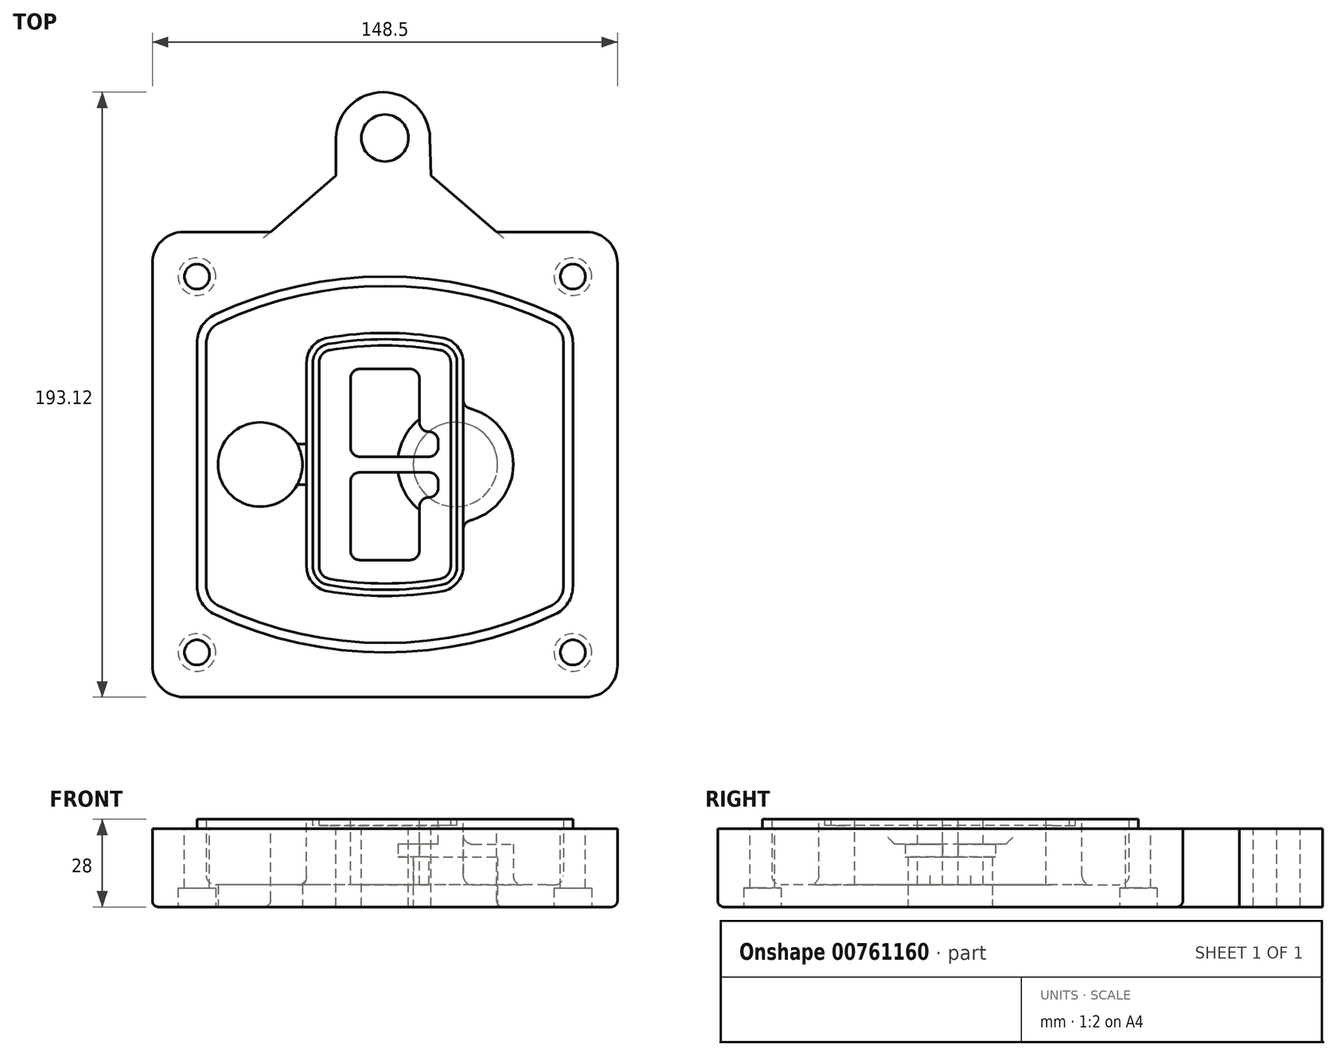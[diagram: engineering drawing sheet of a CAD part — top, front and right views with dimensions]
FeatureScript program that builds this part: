
annotation { "Feature Type Name" : "Feature", "Feature Type Description" : "" }
export const myFeature = defineFeature(function(context is Context, id is Id, definition is map)
    precondition{}
    {
        {
            var Q0;
            Q0=qCreatedBy(makeId("Top.planeOp"),FACE);
            var sketch = newSketch(context, id + "F0", { "sketchPlane" : qUnion([Q0])});
            skPoint(sketch, "E0.rect.middle", {"position": v(0, 0) * mm});
            skLineSegment(sketch, "E1.bottom", {"start": v(-64.25, -74.25) * mm, "end": v(64.25, -74.25) * mm});
            skLineSegment(sketch, "E1.top", {"start": v(-64.25, 74.25) * mm, "end": v(64.25, 74.25) * mm});
            skLineSegment(sketch, "E1.left", {"start": v(-74.25, -64.25) * mm, "end": v(-74.25, 64.25) * mm});
            skLineSegment(sketch, "E1.right", {"start": v(74.25, -64.25) * mm, "end": v(74.25, 64.25) * mm});
            skLineSegment(sketch, "E2", {"start": v(-74.25, 74.25) * mm, "end": v(74.25, -74.25) * mm, "construction": true});
            skLineSegment(sketch, "E3", {"start": v(74.25, 74.25) * mm, "end": v(-74.25, -74.25) * mm, "construction": true});
            skCircle(sketch, "E4", {"center": v(-60, 60) * mm, "radius": 4 * mm});
            skCircle(sketch, "E5", {"center": v(60, 60) * mm, "radius": 4 * mm});
            skCircle(sketch, "E6", {"center": v(60, -60) * mm, "radius": 4 * mm});
            skCircle(sketch, "E7", {"center": v(-60, -60) * mm, "radius": 4 * mm});
            skLineSegment(sketch, "E8", {"start": v(-60, 60) * mm, "end": v(60, 60) * mm, "construction": true});
            skLineSegment(sketch, "E9", {"start": v(60, 60) * mm, "end": v(60, -60) * mm, "construction": true});
            skLineSegment(sketch, "E10", {"start": v(60, -60) * mm, "end": v(-60, -60) * mm, "construction": true});
            skLineSegment(sketch, "E11", {"start": v(-60, -60) * mm, "end": v(-60, 60) * mm, "construction": true});
            skLineSegment(sketch, "E12", {"start": v(-60, 38.83) * mm, "end": v(-60, -38.83) * mm});
            skLineSegment(sketch, "E13", {"start": v(60, 38.83) * mm, "end": v(60, -38.83) * mm});
            skArc(sketch, "E14", {"start": v(54.26, 47.88) * mm, "mid": v(0, 60) * mm, "end": v(-54.26, 47.88) * mm});
            skArc(sketch, "E15", {"start": v(-54.26, -47.88) * mm, "mid": v(0, -60) * mm, "end": v(54.26, -47.88) * mm});
            skLineSegment(sketch, "E16", {"start": v(-60, 0) * mm, "end": v(60, 0) * mm, "construction": true});
            skPoint(sketch, "E17.visualSharp", {"position": v(-60, -45) * mm});
            skArc(sketch, "E17.filletArc", {"start": v(-60, -38.83) * mm, "mid": v(-58.44, -44.2) * mm, "end": v(-54.26, -47.88) * mm});
            skPoint(sketch, "E18.visualSharp", {"position": v(-60, 45) * mm});
            skArc(sketch, "E18.filletArc", {"start": v(-54.26, 47.88) * mm, "mid": v(-58.44, 44.2) * mm, "end": v(-60, 38.83) * mm});
            skPoint(sketch, "E19.visualSharp", {"position": v(60, 45) * mm});
            skArc(sketch, "E19.filletArc", {"start": v(60, 38.83) * mm, "mid": v(58.44, 44.2) * mm, "end": v(54.26, 47.88) * mm});
            skPoint(sketch, "E20.visualSharp", {"position": v(60, -45) * mm});
            skArc(sketch, "E20.filletArc", {"start": v(54.26, -47.88) * mm, "mid": v(58.44, -44.2) * mm, "end": v(60, -38.83) * mm});
            skPoint(sketch, "E21.visualSharp", {"position": v(-74.25, 74.25) * mm});
            skArc(sketch, "E21.filletArc", {"start": v(-64.25, 74.25) * mm, "mid": v(-71.32, 71.32) * mm, "end": v(-74.25, 64.25) * mm});
            skPoint(sketch, "E22.visualSharp", {"position": v(74.25, 74.25) * mm});
            skArc(sketch, "E22.filletArc", {"start": v(74.25, 64.25) * mm, "mid": v(71.32, 71.32) * mm, "end": v(64.25, 74.25) * mm});
            skPoint(sketch, "E23.visualSharp", {"position": v(74.25, -74.25) * mm});
            skArc(sketch, "E23.filletArc", {"start": v(64.25, -74.25) * mm, "mid": v(71.32, -71.32) * mm, "end": v(74.25, -64.25) * mm});
            skPoint(sketch, "E24.visualSharp", {"position": v(-74.25, -74.25) * mm});
            skArc(sketch, "E24.filletArc", {"start": v(-74.25, -64.25) * mm, "mid": v(-71.32, -71.32) * mm, "end": v(-64.25, -74.25) * mm});
            skArc(sketch, "E25.0", {"start": v(57, 38.83) * mm, "mid": v(55.9, 42.58) * mm, "end": v(52.98, 45.17) * mm});
            skLineSegment(sketch, "E25.1", {"start": v(57, 38.83) * mm, "end": v(57, -38.83) * mm});
            skArc(sketch, "E25.2", {"start": v(52.98, -45.17) * mm, "mid": v(55.9, -42.58) * mm, "end": v(57, -38.83) * mm});
            skArc(sketch, "E25.3", {"start": v(-52.98, -45.17) * mm, "mid": v(0, -57) * mm, "end": v(52.98, -45.17) * mm});
            skArc(sketch, "E25.4", {"start": v(-57, -38.83) * mm, "mid": v(-55.9, -42.58) * mm, "end": v(-52.98, -45.17) * mm});
            skArc(sketch, "E25.5", {"start": v(52.98, 45.17) * mm, "mid": v(0, 57) * mm, "end": v(-52.98, 45.17) * mm});
            skLineSegment(sketch, "E25.6", {"start": v(-57, 38.83) * mm, "end": v(-57, -38.83) * mm});
            skArc(sketch, "E25.7", {"start": v(-52.98, 45.17) * mm, "mid": v(-55.9, 42.58) * mm, "end": v(-57, 38.83) * mm});
            skArc(sketch, "E26.0", {"start": v(-55.96, 51.5) * mm, "mid": v(-61.82, 46.33) * mm, "end": v(-64, 38.83) * mm});
            skArc(sketch, "E26.1", {"start": v(55.96, 51.5) * mm, "mid": v(0, 64) * mm, "end": v(-55.96, 51.5) * mm});
            skArc(sketch, "E26.2", {"start": v(64, 38.83) * mm, "mid": v(61.82, 46.33) * mm, "end": v(55.96, 51.5) * mm});
            skLineSegment(sketch, "E26.3", {"start": v(64, 38.83) * mm, "end": v(64, -38.83) * mm});
            skArc(sketch, "E26.4", {"start": v(55.96, -51.5) * mm, "mid": v(61.82, -46.33) * mm, "end": v(64, -38.83) * mm});
            skLineSegment(sketch, "E26.5", {"start": v(-64, 38.83) * mm, "end": v(-64, -38.83) * mm});
            skArc(sketch, "E26.6", {"start": v(-55.96, -51.5) * mm, "mid": v(0, -64) * mm, "end": v(55.96, -51.5) * mm});
            skArc(sketch, "E26.7", {"start": v(-64, -38.83) * mm, "mid": v(-61.82, -46.33) * mm, "end": v(-55.96, -51.5) * mm});
            skCircle(sketch, "E27", {"center": v(0, 104.25) * mm, "radius": 7.5 * mm});
            skPoint(sketch, "E27.centerSnap0", {"position": v(0, 74.25) * mm});
            skArc(sketch, "E28", {"start": v(14.38, 104.25) * mm, "mid": v(-0.61, 118.87) * mm, "end": v(-15.6, 104.25) * mm});
            skLineSegment(sketch, "E29", {"start": v(-15.6, 104.25) * mm, "end": v(-15.6, 92.25) * mm});
            skLineSegment(sketch, "E30", {"start": v(14.38, 104.25) * mm, "end": v(14.7, 92.25) * mm});
            skLineSegment(sketch, "E31", {"start": v(-15.6, 92.25) * mm, "end": v(-36.52, 74.25) * mm});
            skLineSegment(sketch, "E32", {"start": v(14.7, 92.25) * mm, "end": v(35.6, 74.25) * mm});
            skArc(sketch, "E33.MirrorCS", {"start": v(14.38, -252.75) * mm, "mid": v(-0.61, -267.37) * mm, "end": v(-15.6, -252.75) * mm});
            skLineSegment(sketch, "E34.MirrorCS", {"start": v(14.7, -240.75) * mm, "end": v(35.6, -222.75) * mm});
            skLineSegment(sketch, "E35.MirrorCS", {"start": v(-15.6, -240.75) * mm, "end": v(-36.52, -222.75) * mm});
            skLineSegment(sketch, "E36.MirrorCS", {"start": v(14.38, -252.75) * mm, "end": v(14.7, -240.75) * mm});
            skLineSegment(sketch, "E37.MirrorCS", {"start": v(-15.6, -252.75) * mm, "end": v(-15.6, -240.75) * mm});
            skCircle(sketch, "E38.MirrorC", {"center": v(0, -252.75) * mm, "radius": 7.5 * mm});
            skPoint(sketch, "E39.MirrorP", {"position": v(0, -222.75) * mm});
            skSolve(sketch);
        }
        {
            var Q0;
            Q0=makeQuery(id+"F0.imprint","IMPRINT",FACE,{"disambiguationData":[TD([[makeQuery(id+"F0.imprint","IMPRINT",EDGE,{"derivedFrom":sQuery(id+"F0.wireOp",EDGE,"E1.bottom")}),1.0]])]});
            var Q1;
            Q1=makeQuery(id+"F0.imprint","IMPRINT",FACE,{"disambiguationData":[TD([[makeQuery(id+"F0.imprint","IMPRINT",EDGE,{"derivedFrom":sQuery(id+"F0.wireOp",EDGE,"E12")}),1.0]])]});
            var Q2;
            Q2=makeQuery(id+"F0.imprint","IMPRINT",FACE,{"disambiguationData":[TD([[makeQuery(id+"F0.imprint","IMPRINT",EDGE,{"derivedFrom":sQuery(id+"F0.wireOp",EDGE,"E25.0")}),1.0]])]});
            var Q3;
            Q3=makeQuery(id+"F0.imprint","IMPRINT",FACE,{"disambiguationData":[TD([[makeQuery(id+"F0.imprint","IMPRINT",EDGE,{"derivedFrom":sQuery(id+"F0.wireOp",EDGE,"E12")}),-1.0]])]});
            var Q4;
            Q4=makeQuery(id+"F0.imprint","IMPRINT",FACE,{"disambiguationData":[TD([[makeQuery(id+"F0.imprint","IMPRINT",EDGE,{"derivedFrom":sQuery(id+"F0.wireOp",EDGE,"E27")}),-1.0]])]});
            var Q5;
            {var subQ0=sQuery(id+"F0.wireOp",EDGE,"E32");var subQ1=sQuery(id+"F0.wireOp",EDGE,"E1.top");var subQ2=makeQuery(id+"F0.imprint","INTERSECT",VERTEX,{"derivedFrom":[subQ1,subQ0]});Q5=makeQuery(id+"F0.imprint","IMPRINT",FACE,{"disambiguationData":[TD([[makeQuery(id+"F0.imprint","IMPRINT",EDGE,{"disambiguationData":[TD([[subQ2,1.0]])],"derivedFrom":subQ1}),1.0]])]});}
            extrude(context, id + "F1", {"entities" : qUnion([Q0, Q1, Q2, Q3, Q4, Q5]), "oppositeDirection" : true, "depth" : 25 * mm, "offsetDistance" : 25 * mm});
        }
        {
            var Q0;
            Q0=makeQuery(id+"F0.imprint","IMPRINT",FACE,{"disambiguationData":[TD([[makeQuery(id+"F0.imprint","IMPRINT",EDGE,{"derivedFrom":sQuery(id+"F0.wireOp",EDGE,"E12")}),1.0]])]});
            extrude(context, id + "F2", {"entities" : qUnion([Q0]), "operationType" : NewBodyOperationType.ADD, "depth" : 3 * mm});
        }
        {
            var Q0;
            Q0=makeQuery(id+"F0.imprint","IMPRINT",FACE,{"disambiguationData":[TD([[makeQuery(id+"F0.imprint","IMPRINT",EDGE,{"derivedFrom":sQuery(id+"F0.wireOp",EDGE,"E25.0")}),1.0]])]});
            extrude(context, id + "F3", {"entities" : qUnion([Q0]), "operationType" : NewBodyOperationType.REMOVE, "oppositeDirection" : true, "depth" : 18 * mm});
        }
        {
            var Q0;
            Q0=makeQuery(id+"F2.opExtrude","CAP_FACE",FACE,{"disambiguationData":[OSD([sQuery(id+"F0.wireOp",EDGE,"E12"),sQuery(id+"F0.wireOp",EDGE,"E13"),sQuery(id+"F0.wireOp",EDGE,"E14"),sQuery(id+"F0.wireOp",EDGE,"E15"),sQuery(id+"F0.wireOp",EDGE,"E17.filletArc"),sQuery(id+"F0.wireOp",EDGE,"E18.filletArc"),sQuery(id+"F0.wireOp",EDGE,"E19.filletArc"),sQuery(id+"F0.wireOp",EDGE,"E20.filletArc"),sQuery(id+"F0.wireOp",EDGE,"E25.0"),sQuery(id+"F0.wireOp",EDGE,"E25.1"),sQuery(id+"F0.wireOp",EDGE,"E25.2"),sQuery(id+"F0.wireOp",EDGE,"E25.3"),sQuery(id+"F0.wireOp",EDGE,"E25.4"),sQuery(id+"F0.wireOp",EDGE,"E25.5"),sQuery(id+"F0.wireOp",EDGE,"E25.6"),sQuery(id+"F0.wireOp",EDGE,"E25.7")])],"isStart":false});
            var sketch = newSketch(context, id + "F4", { "sketchPlane" : qUnion([Q0])});
            skArc(sketch, "E40.0", {"start": v(-18.34, -40.45) * mm, "mid": v(0, -42) * mm, "end": v(18.34, -40.45) * mm});
            skArc(sketch, "E41.0", {"start": v(18.34, 40.45) * mm, "mid": v(0, 42) * mm, "end": v(-18.34, 40.45) * mm});
            skLineSegment(sketch, "E42", {"start": v(-25, 32.57) * mm, "end": v(-25, -32.57) * mm});
            skLineSegment(sketch, "E43", {"start": v(25, 32.57) * mm, "end": v(25, -32.57) * mm});
            skLineSegment(sketch, "E44", {"start": v(-25, 39.1) * mm, "end": v(25, 39.1) * mm, "construction": true});
            skLineSegment(sketch, "E45", {"start": v(-25, -39.1) * mm, "end": v(25, -39.1) * mm, "construction": true});
            skPoint(sketch, "E46.visualSharp", {"position": v(-25, 39.1) * mm});
            skArc(sketch, "E46.filletArc", {"start": v(-18.34, 40.45) * mm, "mid": v(-23.11, 37.73) * mm, "end": v(-25, 32.57) * mm});
            skPoint(sketch, "E47.visualSharp", {"position": v(25, 39.1) * mm});
            skArc(sketch, "E47.filletArc", {"start": v(25, 32.57) * mm, "mid": v(23.11, 37.73) * mm, "end": v(18.34, 40.45) * mm});
            skPoint(sketch, "E48.visualSharp", {"position": v(25, -39.1) * mm});
            skArc(sketch, "E48.filletArc", {"start": v(18.34, -40.45) * mm, "mid": v(23.11, -37.73) * mm, "end": v(25, -32.57) * mm});
            skPoint(sketch, "E49.visualSharp", {"position": v(-25, -39.1) * mm});
            skArc(sketch, "E49.filletArc", {"start": v(-25, -32.57) * mm, "mid": v(-23.11, -37.73) * mm, "end": v(-18.34, -40.45) * mm});
            skArc(sketch, "E50.0", {"start": v(52.98, 45.17) * mm, "mid": v(0, 57) * mm, "end": v(-52.98, 45.17) * mm});
            skArc(sketch, "E50.1", {"start": v(-52.98, 45.17) * mm, "mid": v(-55.9, 42.58) * mm, "end": v(-57, 38.83) * mm});
            skLineSegment(sketch, "E50.2", {"start": v(-57, 38.83) * mm, "end": v(-57, -38.83) * mm});
            skArc(sketch, "E50.3", {"start": v(-57, -38.83) * mm, "mid": v(-55.9, -42.58) * mm, "end": v(-52.98, -45.17) * mm});
            skArc(sketch, "E50.4", {"start": v(-52.98, -45.17) * mm, "mid": v(0, -57) * mm, "end": v(52.98, -45.17) * mm});
            skArc(sketch, "E50.5", {"start": v(52.98, -45.17) * mm, "mid": v(55.9, -42.58) * mm, "end": v(57, -38.83) * mm});
            skLineSegment(sketch, "E50.6", {"start": v(57, 38.83) * mm, "end": v(57, -38.83) * mm});
            skArc(sketch, "E50.7", {"start": v(57, 38.83) * mm, "mid": v(55.9, 42.58) * mm, "end": v(52.98, 45.17) * mm});
            skLineSegment(sketch, "E51.0", {"start": v(23, 32.57) * mm, "end": v(23, -32.57) * mm});
            skArc(sketch, "E51.1", {"start": v(18, -38.48) * mm, "mid": v(21.58, -36.44) * mm, "end": v(23, -32.57) * mm});
            skArc(sketch, "E51.2", {"start": v(-18, -38.48) * mm, "mid": v(0, -40) * mm, "end": v(18, -38.48) * mm});
            skArc(sketch, "E51.3", {"start": v(-23, -32.57) * mm, "mid": v(-21.58, -36.44) * mm, "end": v(-18, -38.48) * mm});
            skLineSegment(sketch, "E51.4", {"start": v(-23, 32.57) * mm, "end": v(-23, -32.57) * mm});
            skArc(sketch, "E51.5", {"start": v(23, 32.57) * mm, "mid": v(21.58, 36.44) * mm, "end": v(18, 38.48) * mm});
            skArc(sketch, "E51.6", {"start": v(-18, 38.48) * mm, "mid": v(-21.58, 36.44) * mm, "end": v(-23, 32.57) * mm});
            skArc(sketch, "E51.7", {"start": v(18, 38.48) * mm, "mid": v(0, 40) * mm, "end": v(-18, 38.48) * mm});
            skArc(sketch, "E52.0", {"start": v(21, 32.57) * mm, "mid": v(20.06, 35.15) * mm, "end": v(17.67, 36.5) * mm});
            skLineSegment(sketch, "E52.1", {"start": v(21, 32.57) * mm, "end": v(21, -32.57) * mm});
            skArc(sketch, "E52.2", {"start": v(17.67, -36.5) * mm, "mid": v(20.06, -35.15) * mm, "end": v(21, -32.57) * mm});
            skArc(sketch, "E52.3", {"start": v(-17.67, -36.5) * mm, "mid": v(0, -38) * mm, "end": v(17.67, -36.5) * mm});
            skArc(sketch, "E52.4", {"start": v(-21, -32.57) * mm, "mid": v(-20.06, -35.15) * mm, "end": v(-17.67, -36.5) * mm});
            skArc(sketch, "E52.5", {"start": v(17.67, 36.5) * mm, "mid": v(0, 38) * mm, "end": v(-17.67, 36.5) * mm});
            skLineSegment(sketch, "E52.6", {"start": v(-21, 32.57) * mm, "end": v(-21, -32.57) * mm});
            skArc(sketch, "E52.7", {"start": v(-17.67, 36.5) * mm, "mid": v(-20.06, 35.15) * mm, "end": v(-21, 32.57) * mm});
            skLineSegment(sketch, "E53", {"start": v(-25, 0) * mm, "end": v(25, 0) * mm, "construction": true});
            skLineSegment(sketch, "E54", {"start": v(-11, 5.5) * mm, "end": v(-11, 27.5) * mm});
            skLineSegment(sketch, "E55", {"start": v(-8, 30.5) * mm, "end": v(8, 30.5) * mm});
            skLineSegment(sketch, "E56", {"start": v(11, 27.5) * mm, "end": v(11, 13.5) * mm});
            skLineSegment(sketch, "E57", {"start": v(14, 10.5) * mm, "end": v(14, 10.5) * mm});
            skLineSegment(sketch, "E58", {"start": v(17, 7.5) * mm, "end": v(17, 5.5) * mm});
            skLineSegment(sketch, "E59", {"start": v(14, 2.5) * mm, "end": v(-8, 2.5) * mm});
            skPoint(sketch, "E60.visualSharp", {"position": v(-11, 30.5) * mm});
            skArc(sketch, "E60.filletArc", {"start": v(-8, 30.5) * mm, "mid": v(-10.12, 29.62) * mm, "end": v(-11, 27.5) * mm});
            skPoint(sketch, "E61.visualSharp", {"position": v(11, 30.5) * mm});
            skArc(sketch, "E61.filletArc", {"start": v(11, 27.5) * mm, "mid": v(10.12, 29.62) * mm, "end": v(8, 30.5) * mm});
            skPoint(sketch, "E62.visualSharp", {"position": v(11, 10.5) * mm});
            skArc(sketch, "E62.filletArc", {"start": v(11, 13.5) * mm, "mid": v(11.88, 11.38) * mm, "end": v(14, 10.5) * mm});
            skPoint(sketch, "E63.visualSharp", {"position": v(17, 10.5) * mm});
            skArc(sketch, "E63.filletArc", {"start": v(17, 7.5) * mm, "mid": v(16.12, 9.62) * mm, "end": v(14, 10.5) * mm});
            skPoint(sketch, "E64.visualSharp", {"position": v(17, 2.5) * mm});
            skArc(sketch, "E64.filletArc", {"start": v(14, 2.5) * mm, "mid": v(16.12, 3.38) * mm, "end": v(17, 5.5) * mm});
            skPoint(sketch, "E65.visualSharp", {"position": v(-11, 2.5) * mm});
            skArc(sketch, "E65.filletArc", {"start": v(-11, 5.5) * mm, "mid": v(-10.12, 3.38) * mm, "end": v(-8, 2.5) * mm});
            skLineSegment(sketch, "E66.0.MirrorCS", {"start": v(14, -2.5) * mm, "end": v(-8, -2.5) * mm});
            skArc(sketch, "E67.0.MirrorCS", {"start": v(-11, -5.5) * mm, "mid": v(-10.12, -3.38) * mm, "end": v(-8, -2.5) * mm});
            skLineSegment(sketch, "E68.0.MirrorCS", {"start": v(-11, -5.5) * mm, "end": v(-11, -27.5) * mm});
            skArc(sketch, "E69.0.MirrorCS", {"start": v(-8, -30.5) * mm, "mid": v(-10.12, -29.62) * mm, "end": v(-11, -27.5) * mm});
            skLineSegment(sketch, "E70.0.MirrorCS", {"start": v(-8, -30.5) * mm, "end": v(8, -30.5) * mm});
            skArc(sketch, "E71.0.MirrorCS", {"start": v(11, -27.5) * mm, "mid": v(10.12, -29.62) * mm, "end": v(8, -30.5) * mm});
            skLineSegment(sketch, "E72.0.MirrorCS", {"start": v(11, -27.5) * mm, "end": v(11, -13.5) * mm});
            skArc(sketch, "E73.0.MirrorCS", {"start": v(11, -13.5) * mm, "mid": v(11.88, -11.38) * mm, "end": v(14, -10.5) * mm});
            skArc(sketch, "E74.0.MirrorCS", {"start": v(17, -7.5) * mm, "mid": v(16.12, -9.62) * mm, "end": v(14, -10.5) * mm});
            skLineSegment(sketch, "E75.0.MirrorCS", {"start": v(17, -7.5) * mm, "end": v(17, -5.5) * mm});
            skArc(sketch, "E76.0.MirrorCS", {"start": v(14, -2.5) * mm, "mid": v(16.12, -3.38) * mm, "end": v(17, -5.5) * mm});
            skSolve(sketch);
        }
        {
            var Q0;
            Q0=makeQuery(id+"F4.imprint","IMPRINT",FACE,{"disambiguationData":[TD([[makeQuery(id+"F4.imprint","IMPRINT",EDGE,{"derivedFrom":sQuery(id+"F4.wireOp",EDGE,"E40.0")}),1.0]])]});
            var Q1;
            Q1=makeQuery(id+"F4.imprint","IMPRINT",FACE,{"disambiguationData":[TD([[makeQuery(id+"F4.imprint","IMPRINT",EDGE,{"derivedFrom":sQuery(id+"F4.wireOp",EDGE,"E51.0")}),-1.0]])]});
            var Q2;
            Q2=makeQuery(id+"F4.imprint","IMPRINT",FACE,{"disambiguationData":[TD([[makeQuery(id+"F4.imprint","IMPRINT",EDGE,{"derivedFrom":sQuery(id+"F4.wireOp",EDGE,"E52.0")}),1.0]])]});
            extrude(context, id + "F5", {"entities" : qUnion([Q0, Q1, Q2]), "operationType" : NewBodyOperationType.ADD, "endBound" : BoundingType.UP_TO_NEXT, "oppositeDirection" : true, "depth" : 25 * mm});
        }
        {
            var Q0;
            Q0=makeQuery(id+"F4.imprint","IMPRINT",FACE,{"disambiguationData":[TD([[makeQuery(id+"F4.imprint","IMPRINT",EDGE,{"derivedFrom":sQuery(id+"F4.wireOp",EDGE,"E51.0")}),-1.0]])]});
            extrude(context, id + "F6", {"entities" : qUnion([Q0]), "operationType" : NewBodyOperationType.REMOVE, "oppositeDirection" : true, "depth" : 2 * mm});
        }
        {
            var Q0;
            Q0=makeQuery(id+"F1.opExtrude","CAP_FACE",FACE,{"disambiguationData":[OSD([sQuery(id+"F0.wireOp",EDGE,"E1.bottom"),sQuery(id+"F0.wireOp",EDGE,"E1.top"),sQuery(id+"F0.wireOp",EDGE,"E1.left"),sQuery(id+"F0.wireOp",EDGE,"E1.right"),sQuery(id+"F0.wireOp",EDGE,"E4"),sQuery(id+"F0.wireOp",EDGE,"E5"),sQuery(id+"F0.wireOp",EDGE,"E6"),sQuery(id+"F0.wireOp",EDGE,"E7"),sQuery(id+"F0.wireOp",EDGE,"E21.filletArc"),sQuery(id+"F0.wireOp",EDGE,"E22.filletArc"),sQuery(id+"F0.wireOp",EDGE,"E23.filletArc"),sQuery(id+"F0.wireOp",EDGE,"E24.filletArc")])],"isStart":false});
            var sketch = newSketch(context, id + "F7", { "sketchPlane" : qUnion([Q0])});
            skCircle(sketch, "E77", {"center": v(22.5, 0) * mm, "radius": 13.47 * mm});
            skCircle(sketch, "E78", {"center": v(-39.81, 0) * mm, "radius": 13.47 * mm});
            skLineSegment(sketch, "E79", {"start": v(74.25, 0) * mm, "end": v(-74.25, 0) * mm});
            skCircle(sketch, "E80", {"center": v(22.5, 0) * mm, "radius": 18.47 * mm});
            skCircle(sketch, "E81", {"center": v(60, -60) * mm, "radius": 6 * mm});
            skCircle(sketch, "E82", {"center": v(-60, -60) * mm, "radius": 6 * mm});
            skCircle(sketch, "E83", {"center": v(-60, 60) * mm, "radius": 6 * mm});
            skCircle(sketch, "E84", {"center": v(60, 60) * mm, "radius": 6 * mm});
            skSolve(sketch);
        }
        {
            var Q0;
            {var subQ1=sQuery(id+"F7.wireOp",EDGE,"E79");var subQ4=sQuery(id+"F7.wireOp",EDGE,"E77");var subQ6=makeQuery(id+"F7.imprint","INTERSECT",VERTEX,{"disambiguationData":[OD(0.0)],"derivedFrom":[subQ4,subQ1]});Q0=makeQuery(id+"F7.imprint","IMPRINT",FACE,{"disambiguationData":[TD([[makeQuery(id+"F7.imprint","IMPRINT",EDGE,{"disambiguationData":[TD([[subQ6,-1.0]])],"derivedFrom":subQ4}),-1.0]])]});}
            var Q1;
            {var subQ0=sQuery(id+"F7.wireOp",EDGE,"E79");var subQ1=sQuery(id+"F7.wireOp",EDGE,"E77");var subQ3=makeQuery(id+"F7.imprint","INTERSECT",VERTEX,{"disambiguationData":[OD(0.0)],"derivedFrom":[subQ1,subQ0]});Q1=makeQuery(id+"F7.imprint","IMPRINT",FACE,{"disambiguationData":[TD([[makeQuery(id+"F7.imprint","IMPRINT",EDGE,{"disambiguationData":[TD([[subQ3,-1.0]])],"derivedFrom":subQ1}),1.0]])]});}
            var Q2;
            {var subQ0=sQuery(id+"F7.wireOp",EDGE,"E79");var subQ1=sQuery(id+"F7.wireOp",EDGE,"E77");var subQ3=makeQuery(id+"F7.imprint","INTERSECT",VERTEX,{"disambiguationData":[OD(0.0)],"derivedFrom":[subQ1,subQ0]});Q2=makeQuery(id+"F7.imprint","IMPRINT",FACE,{"disambiguationData":[TD([[makeQuery(id+"F7.imprint","IMPRINT",EDGE,{"disambiguationData":[TD([[subQ3,1.0]])],"derivedFrom":subQ1}),1.0]])]});}
            var Q3;
            {var subQ1=sQuery(id+"F7.wireOp",EDGE,"E79");var subQ4=sQuery(id+"F7.wireOp",EDGE,"E77");var subQ6=makeQuery(id+"F7.imprint","INTERSECT",VERTEX,{"disambiguationData":[OD(0.0)],"derivedFrom":[subQ4,subQ1]});Q3=makeQuery(id+"F7.imprint","IMPRINT",FACE,{"disambiguationData":[TD([[makeQuery(id+"F7.imprint","IMPRINT",EDGE,{"disambiguationData":[TD([[subQ6,1.0]])],"derivedFrom":subQ4}),-1.0]])]});}
            extrude(context, id + "F8", {"entities" : qUnion([Q0, Q1, Q2, Q3]), "operationType" : NewBodyOperationType.ADD, "oppositeDirection" : true, "depth" : 20 * mm});
        }
        {
            var Q0;
            {var subQ0=sQuery(id+"F7.wireOp",EDGE,"E79");var subQ1=sQuery(id+"F7.wireOp",EDGE,"E77");var subQ3=makeQuery(id+"F7.imprint","INTERSECT",VERTEX,{"disambiguationData":[OD(0.0)],"derivedFrom":[subQ1,subQ0]});Q0=makeQuery(id+"F7.imprint","IMPRINT",FACE,{"disambiguationData":[TD([[makeQuery(id+"F7.imprint","IMPRINT",EDGE,{"disambiguationData":[TD([[subQ3,-1.0]])],"derivedFrom":subQ1}),1.0]])]});}
            var Q1;
            {var subQ0=sQuery(id+"F7.wireOp",EDGE,"E79");var subQ1=sQuery(id+"F7.wireOp",EDGE,"E77");var subQ3=makeQuery(id+"F7.imprint","INTERSECT",VERTEX,{"disambiguationData":[OD(0.0)],"derivedFrom":[subQ1,subQ0]});Q1=makeQuery(id+"F7.imprint","IMPRINT",FACE,{"disambiguationData":[TD([[makeQuery(id+"F7.imprint","IMPRINT",EDGE,{"disambiguationData":[TD([[subQ3,1.0]])],"derivedFrom":subQ1}),1.0]])]});}
            extrude(context, id + "F9", {"entities" : qUnion([Q0, Q1]), "operationType" : NewBodyOperationType.REMOVE, "oppositeDirection" : true, "depth" : 16 * mm});
        }
        {
            var Q0;
            {var subQ0=sQuery(id+"F7.wireOp",EDGE,"E79");var subQ1=sQuery(id+"F7.wireOp",EDGE,"E78");var subQ3=makeQuery(id+"F7.imprint","INTERSECT",VERTEX,{"disambiguationData":[OD(0.0)],"derivedFrom":[subQ1,subQ0]});Q0=makeQuery(id+"F7.imprint","IMPRINT",FACE,{"disambiguationData":[TD([[makeQuery(id+"F7.imprint","IMPRINT",EDGE,{"disambiguationData":[TD([[subQ3,-1.0]])],"derivedFrom":subQ1}),1.0]])]});}
            var Q1;
            {var subQ0=sQuery(id+"F7.wireOp",EDGE,"E79");var subQ1=sQuery(id+"F7.wireOp",EDGE,"E78");var subQ3=makeQuery(id+"F7.imprint","INTERSECT",VERTEX,{"disambiguationData":[OD(0.0)],"derivedFrom":[subQ1,subQ0]});Q1=makeQuery(id+"F7.imprint","IMPRINT",FACE,{"disambiguationData":[TD([[makeQuery(id+"F7.imprint","IMPRINT",EDGE,{"disambiguationData":[TD([[subQ3,1.0]])],"derivedFrom":subQ1}),1.0]])]});}
            extrude(context, id + "F10", {"entities" : qUnion([Q0, Q1]), "operationType" : NewBodyOperationType.REMOVE, "oppositeDirection" : true, "depth" : 25 * mm});
        }
        {
            var Q0;
            Q0=makeQuery(id+"F7.imprint","IMPRINT",FACE,{"disambiguationData":[TD([[makeQuery(id+"F7.imprint","IMPRINT",EDGE,{"derivedFrom":sQuery(id+"F7.wireOp",EDGE,"E81")}),1.0]])]});
            var Q1;
            Q1=makeQuery(id+"F7.imprint","IMPRINT",FACE,{"disambiguationData":[TD([[makeQuery(id+"F7.imprint","IMPRINT",EDGE,{"derivedFrom":makeQuery(id+"F1.opExtrude","CAP_EDGE",EDGE,{"disambiguationData":[OSD([sQuery(id+"F0.wireOp",EDGE,"E5")])],"isStart":false})}),-1.0]])]});
            var Q2;
            Q2=makeQuery(id+"F7.imprint","IMPRINT",FACE,{"disambiguationData":[TD([[makeQuery(id+"F7.imprint","IMPRINT",EDGE,{"derivedFrom":sQuery(id+"F7.wireOp",EDGE,"E82")}),1.0]])]});
            var Q3;
            Q3=makeQuery(id+"F7.imprint","IMPRINT",FACE,{"disambiguationData":[TD([[makeQuery(id+"F7.imprint","IMPRINT",EDGE,{"derivedFrom":makeQuery(id+"F1.opExtrude","CAP_EDGE",EDGE,{"disambiguationData":[OSD([sQuery(id+"F0.wireOp",EDGE,"E4")])],"isStart":false})}),-1.0]])]});
            var Q4;
            Q4=makeQuery(id+"F7.imprint","IMPRINT",FACE,{"disambiguationData":[TD([[makeQuery(id+"F7.imprint","IMPRINT",EDGE,{"derivedFrom":sQuery(id+"F7.wireOp",EDGE,"E83")}),1.0]])]});
            var Q5;
            Q5=makeQuery(id+"F7.imprint","IMPRINT",FACE,{"disambiguationData":[TD([[makeQuery(id+"F7.imprint","IMPRINT",EDGE,{"derivedFrom":makeQuery(id+"F1.opExtrude","CAP_EDGE",EDGE,{"disambiguationData":[OSD([sQuery(id+"F0.wireOp",EDGE,"E7")])],"isStart":false})}),-1.0]])]});
            var Q6;
            Q6=makeQuery(id+"F7.imprint","IMPRINT",FACE,{"disambiguationData":[TD([[makeQuery(id+"F7.imprint","IMPRINT",EDGE,{"derivedFrom":sQuery(id+"F7.wireOp",EDGE,"E84")}),1.0]])]});
            var Q7;
            Q7=makeQuery(id+"F7.imprint","IMPRINT",FACE,{"disambiguationData":[TD([[makeQuery(id+"F7.imprint","IMPRINT",EDGE,{"derivedFrom":makeQuery(id+"F1.opExtrude","CAP_EDGE",EDGE,{"disambiguationData":[OSD([sQuery(id+"F0.wireOp",EDGE,"E6")])],"isStart":false})}),-1.0]])]});
            extrude(context, id + "F11", {"entities" : qUnion([Q0, Q1, Q2, Q3, Q4, Q5, Q6, Q7]), "operationType" : NewBodyOperationType.REMOVE, "oppositeDirection" : true, "depth" : 6 * mm});
        }
        {
            var Q0;
            Q0=makeQuery(id+"F9.boolean.opBoolean","COPY",FACE,{"derivedFrom":makeQuery(id+"F9.opExtrude","CAP_FACE",FACE,{"disambiguationData":[OSD([sQuery(id+"F7.wireOp",EDGE,"E77")])],"isStart":false})});
            var sketch = newSketch(context, id + "F12", { "sketchPlane" : qUnion([Q0])});
            skArc(sketch, "E85.0", {"start": v(11, 14.45) * mm, "mid": v(6.45, 9.13) * mm, "end": v(4.2, 2.5) * mm});
            skArc(sketch, "E85.1", {"start": v(4.2, -2.5) * mm, "mid": v(6.45, -9.13) * mm, "end": v(11, -14.45) * mm});
            skLineSegment(sketch, "E86", {"start": v(4.2, -2.5) * mm, "end": v(14, -2.5) * mm});
            skLineSegment(sketch, "E87.0", {"start": v(14, 2.5) * mm, "end": v(4.2, 2.5) * mm});
            skArc(sketch, "E87.1", {"start": v(14, 2.5) * mm, "mid": v(16.12, 3.38) * mm, "end": v(17, 5.5) * mm});
            skLineSegment(sketch, "E87.2", {"start": v(17, 7.5) * mm, "end": v(17, 5.5) * mm});
            skArc(sketch, "E87.3", {"start": v(17, 7.5) * mm, "mid": v(16.12, 9.62) * mm, "end": v(14, 10.5) * mm});
            skArc(sketch, "E87.4", {"start": v(11, 13.5) * mm, "mid": v(11.88, 11.38) * mm, "end": v(14, 10.5) * mm});
            skLineSegment(sketch, "E87.5", {"start": v(11, 14.45) * mm, "end": v(11, 13.5) * mm});
            skLineSegment(sketch, "E87.7", {"start": v(14, -2.5) * mm, "end": v(4.2, -2.5) * mm});
            skArc(sketch, "E87.8", {"start": v(14, -2.5) * mm, "mid": v(16.12, -3.38) * mm, "end": v(17, -5.5) * mm});
            skLineSegment(sketch, "E87.9", {"start": v(17, -7.5) * mm, "end": v(17, -5.5) * mm});
            skArc(sketch, "E87.10", {"start": v(17, -7.5) * mm, "mid": v(16.12, -9.62) * mm, "end": v(14, -10.5) * mm});
            skArc(sketch, "E87.11", {"start": v(11, -13.5) * mm, "mid": v(11.88, -11.38) * mm, "end": v(14, -10.5) * mm});
            skLineSegment(sketch, "E87.12", {"start": v(11, -14.45) * mm, "end": v(11, -13.5) * mm});
            skPoint(sketch, "E88.orphan", {"position": v(11, -27.5) * mm});
            skPoint(sketch, "E89.orphan", {"position": v(-8, -2.5) * mm});
            skPoint(sketch, "E90.orphan", {"position": v(-8, 2.5) * mm});
            skPoint(sketch, "E91.orphan", {"position": v(11, 27.5) * mm});
            skSolve(sketch);
        }
        {
            var Q0;
            {var subQ7=sQuery(id+"F12.wireOp",EDGE,"E85.0");var subQ14=sQuery(id+"F12.wireOp",EDGE,"E85.1");var subQ16=sQuery(id+"F12.wireOp",EDGE,"E87.1");var subQ18=sQuery(id+"F12.wireOp",EDGE,"E87.8");Q0=qUnion([makeQuery(id+"F12.imprint","IMPRINT",FACE,{"disambiguationData":[TD([[makeQuery(id+"F12.imprint","IMPRINT",EDGE,{"derivedFrom":subQ7}),1.0]])]}),makeQuery(id+"F12.imprint","IMPRINT",FACE,{"disambiguationData":[TD([[makeQuery(id+"F12.imprint","IMPRINT",EDGE,{"derivedFrom":subQ14}),1.0]])]}),makeQuery(id+"F12.imprint","IMPRINT",FACE,{"disambiguationData":[TD([[makeQuery(id+"F12.imprint","IMPRINT",EDGE,{"derivedFrom":subQ16}),1.0]])]}),makeQuery(id+"F12.imprint","IMPRINT",FACE,{"disambiguationData":[TD([[makeQuery(id+"F12.imprint","IMPRINT",EDGE,{"derivedFrom":subQ18}),-1.0]])]})]);}
            var Q1;
            Q1=makeQuery(id+"F5.boolean.opBoolean","SPLIT",FACE,{"disambiguationData":[TD([makeQuery(id+"F5.opExtrude","SWEPT_FACE",FACE,{"disambiguationData":[OSD([sQuery(id+"F4.wireOp",EDGE,"E54")])]})])],"derivedFrom":makeQuery(id+"F3.boolean.opBoolean","COPY",FACE,{"derivedFrom":makeQuery(id+"F3.opExtrude","CAP_FACE",FACE,{"disambiguationData":[OSD([sQuery(id+"F0.wireOp",EDGE,"E25.0"),sQuery(id+"F0.wireOp",EDGE,"E25.1"),sQuery(id+"F0.wireOp",EDGE,"E25.2"),sQuery(id+"F0.wireOp",EDGE,"E25.3"),sQuery(id+"F0.wireOp",EDGE,"E25.4"),sQuery(id+"F0.wireOp",EDGE,"E25.5"),sQuery(id+"F0.wireOp",EDGE,"E25.6"),sQuery(id+"F0.wireOp",EDGE,"E25.7")])],"isStart":false})})});
            extrude(context, id + "F13", {"entities" : qUnion([Q0]), "operationType" : NewBodyOperationType.REMOVE, "endBound" : BoundingType.UP_TO_SURFACE, "endBoundEntityFace" : qUnion([Q1]), "depth" : 25 * mm});
        }
        {
            var Q0;
            Q0=makeQuery(id+"F3.boolean.opBoolean","COPY",EDGE,{"derivedFrom":makeQuery(id+"F3.opExtrude","CAP_EDGE",EDGE,{"disambiguationData":[OSD([sQuery(id+"F0.wireOp",EDGE,"E25.6")])],"isStart":false})});
            var Q1;
            Q1=makeQuery(id+"F8.boolean.opBoolean","INTERSECT",EDGE,{"derivedFrom":[makeQuery(id+"F5.opExtrude","SWEPT_FACE",FACE,{"disambiguationData":[OSD([sQuery(id+"F4.wireOp",EDGE,"E43")])]}),makeQuery(id+"F8.opExtrude","CAP_FACE",FACE,{"disambiguationData":[OSD([sQuery(id+"F7.wireOp",EDGE,"E80")])],"isStart":false})]});
            var Q2;
            Q2=makeQuery(id+"F8.boolean.opBoolean","INTERSECT",EDGE,{"disambiguationData":[OD(1.0)],"derivedFrom":[makeQuery(id+"F5.opExtrude","SWEPT_FACE",FACE,{"disambiguationData":[OSD([sQuery(id+"F4.wireOp",EDGE,"E43")])]}),makeQuery(id+"F8.opExtrude","SWEPT_FACE",FACE,{"disambiguationData":[OSD([sQuery(id+"F7.wireOp",EDGE,"E80")])]})]});
            var Q3;
            {var subQ0=sQuery(id+"F4.wireOp",EDGE,"E43");Q3=makeQuery(id+"F8.boolean.opBoolean","SPLIT",EDGE,{"disambiguationData":[TD([makeQuery(id+"F5.opExtrude","SWEPT_FACE",FACE,{"disambiguationData":[OSD([sQuery(id+"F4.wireOp",EDGE,"E48.filletArc")])]})])],"derivedFrom":makeQuery(id+"F5.opExtrude","CAP_EDGE",EDGE,{"disambiguationData":[OSD([subQ0])],"isStart":false})});}
            var Q4;
            {var subQ0=sQuery(id+"F0.wireOp",EDGE,"E25.7");var subQ1=sQuery(id+"F0.wireOp",EDGE,"E25.1");var subQ2=sQuery(id+"F0.wireOp",EDGE,"E25.6");var subQ3=sQuery(id+"F0.wireOp",EDGE,"E25.5");var subQ4=sQuery(id+"F0.wireOp",EDGE,"E25.4");var subQ5=sQuery(id+"F0.wireOp",EDGE,"E25.0");var subQ6=sQuery(id+"F0.wireOp",EDGE,"E25.2");var subQ7=sQuery(id+"F0.wireOp",EDGE,"E25.3");Q4=makeQuery(id+"F8.boolean.opBoolean","INTERSECT",EDGE,{"derivedFrom":[makeQuery(id+"F5.boolean.opBoolean","SPLIT",FACE,{"disambiguationData":[TD([makeQuery(id+"F2.opExtrude","SWEPT_FACE",FACE,{"disambiguationData":[OSD([subQ5])]})])],"derivedFrom":makeQuery(id+"F3.boolean.opBoolean","COPY",FACE,{"derivedFrom":makeQuery(id+"F3.opExtrude","CAP_FACE",FACE,{"disambiguationData":[OSD([subQ5,subQ1,subQ6,subQ7,subQ4,subQ3,subQ2,subQ0])],"isStart":false})})}),makeQuery(id+"F8.opExtrude","SWEPT_FACE",FACE,{"disambiguationData":[OSD([sQuery(id+"F7.wireOp",EDGE,"E80")])]})]});}
            var Q5;
            Q5=makeQuery(id+"F8.boolean.opBoolean","INTERSECT",EDGE,{"disambiguationData":[OD(0.0)],"derivedFrom":[makeQuery(id+"F5.opExtrude","SWEPT_FACE",FACE,{"disambiguationData":[OSD([sQuery(id+"F4.wireOp",EDGE,"E43")])]}),makeQuery(id+"F8.opExtrude","SWEPT_FACE",FACE,{"disambiguationData":[OSD([sQuery(id+"F7.wireOp",EDGE,"E80")])]})]});
            fillet(context, id + "F14", {"entities" : qUnion([Q0, Q1, Q2, Q3, Q4, Q5]), "radius" : 3 * mm, "tangentPropagation" : true, "allowEdgeOverflow" : false});
        }
        {
            var Q0;
            Q0=makeQuery(id+"F1.opExtrude","CAP_EDGE",EDGE,{"disambiguationData":[OSD([sQuery(id+"F0.wireOp",EDGE,"E1.bottom")])],"isStart":false});
            fillet(context, id + "F15", {"entities" : qUnion([Q0]), "radius" : 2 * mm, "tangentPropagation" : true, "allowEdgeOverflow" : false});
        }
    });
